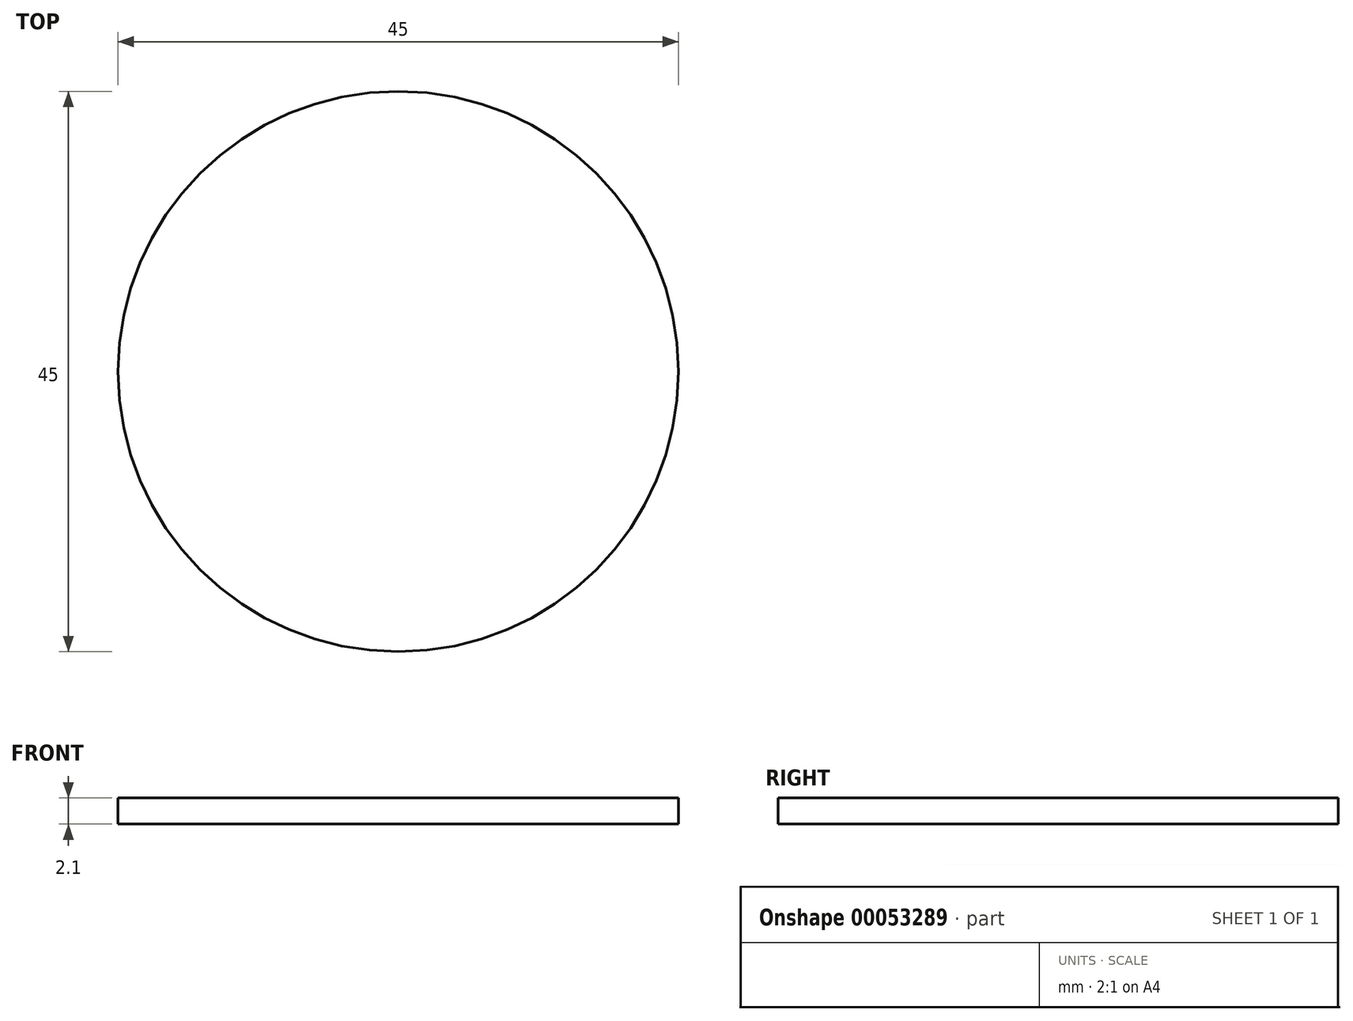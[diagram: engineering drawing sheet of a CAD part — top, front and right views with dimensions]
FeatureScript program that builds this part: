
annotation { "Feature Type Name" : "Feature", "Feature Type Description" : "" }
export const myFeature = defineFeature(function(context is Context, id is Id, definition is map)
    precondition{}
    {
        {
            var Q0;
            Q0=qCreatedBy(makeId("Top.planeOp"),FACE);
            var sketch = newSketch(context, id + "F0", { "sketchPlane" : qUnion([Q0])});
            skCircle(sketch, "E0", {"center": v(0, 0) * mm, "radius": 22.5 * mm});
            skSolve(sketch);
        }
        {
            var Q0;
            Q0 = qSketchRegion(id + "F0", true);
            extrude(context, id + "F1", {"entities" : qUnion([Q0]), "depth" : 2.1 * mm});
        }
    });
